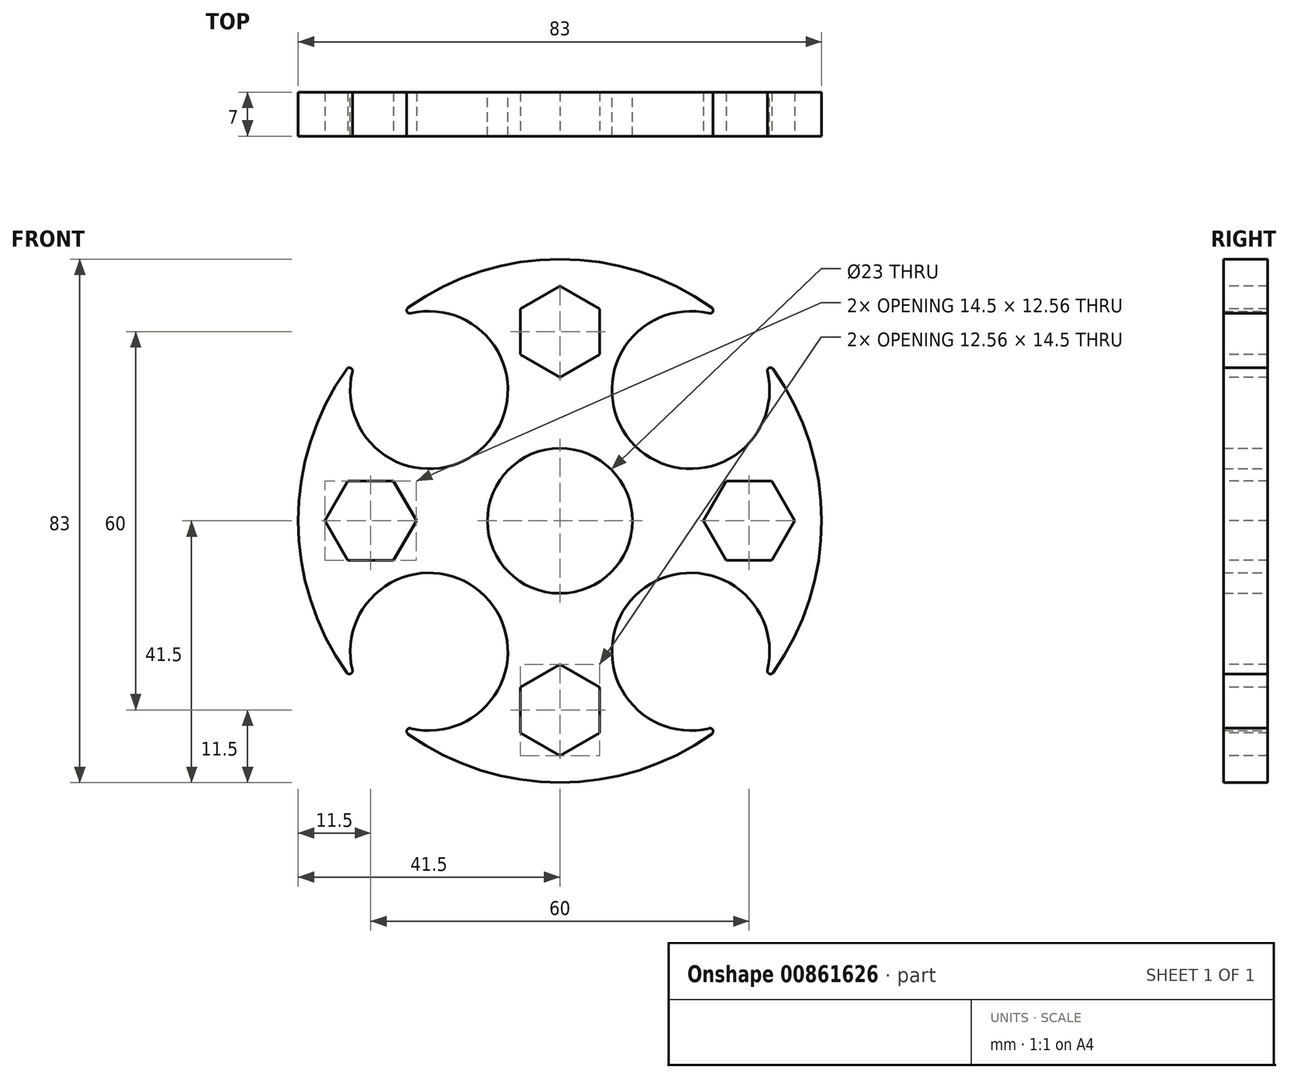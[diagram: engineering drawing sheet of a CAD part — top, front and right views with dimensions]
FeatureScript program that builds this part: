
annotation { "Feature Type Name" : "Feature", "Feature Type Description" : "" }
export const myFeature = defineFeature(function(context is Context, id is Id, definition is map)
    precondition{}
    {
        {
            var Q0;
            Q0=qCreatedBy(makeId("Front.planeOp"),FACE);
            var sketch = newSketch(context, id + "F0", { "sketchPlane" : qUnion([Q0])});
            skCircle(sketch, "E0", {"center": v(0, 0) * mm, "radius": 11.5 * mm});
            skCircle(sketch, "E1", {"center": v(0, 0) * mm, "radius": 41.5 * mm});
            skLineSegment(sketch, "E2", {"start": v(0, 0) * mm, "end": v(0, 41.5) * mm});
            skLineSegment(sketch, "E3", {"start": v(0, 0) * mm, "end": v(41.5, 0) * mm});
            skLineSegment(sketch, "E4", {"start": v(0, 0) * mm, "end": v(0, -41.5) * mm});
            skLineSegment(sketch, "E5", {"start": v(0, 0) * mm, "end": v(-41.5, 0) * mm});
            skLineSegment(sketch, "E6", {"start": v(-20.75, 0) * mm, "end": v(-20.75, 35.94) * mm});
            skLineSegment(sketch, "E7", {"start": v(0, 20.75) * mm, "end": v(-35.94, 20.75) * mm});
            skLineSegment(sketch, "E8", {"start": v(0, 20.75) * mm, "end": v(35.94, 20.75) * mm});
            skLineSegment(sketch, "E9", {"start": v(20.75, 0) * mm, "end": v(20.75, 35.94) * mm});
            skLineSegment(sketch, "E10", {"start": v(0, -20.75) * mm, "end": v(35.94, -20.75) * mm});
            skLineSegment(sketch, "E11", {"start": v(20.75, 0) * mm, "end": v(20.75, -35.94) * mm});
            skLineSegment(sketch, "E12", {"start": v(-20.75, 0) * mm, "end": v(-20.75, -35.94) * mm});
            skLineSegment(sketch, "E13", {"start": v(0, -20.75) * mm, "end": v(-35.94, -20.75) * mm});
            skCircle(sketch, "E14", {"center": v(-20.75, 20.75) * mm, "radius": 12.5 * mm});
            skCircle(sketch, "E15", {"center": v(20.75, 20.75) * mm, "radius": 12.5 * mm});
            skCircle(sketch, "E16", {"center": v(-20.75, -20.75) * mm, "radius": 12.5 * mm});
            skCircle(sketch, "E17", {"center": v(20.75, -20.75) * mm, "radius": 12.5 * mm});
            skSolve(sketch);
        }
        {
            var Q0;
            {var subQ1=sQuery(id+"F0.wireOp",EDGE,"E2");var subQ5=sQuery(id+"F0.wireOp",EDGE,"E1");var subQ6=makeQuery(id+"F0.imprint","INTERSECT",VERTEX,{"derivedFrom":[subQ5,subQ1]});Q0=makeQuery(id+"F0.imprint","IMPRINT",FACE,{"disambiguationData":[TD([[makeQuery(id+"F0.imprint","IMPRINT",EDGE,{"disambiguationData":[TD([[subQ6,-1.0]])],"derivedFrom":subQ5}),1.0]])]});}
            var Q1;
            {var subQ1=sQuery(id+"F0.wireOp",EDGE,"E2");var subQ7=sQuery(id+"F0.wireOp",EDGE,"E1");var subQ9=makeQuery(id+"F0.imprint","INTERSECT",VERTEX,{"derivedFrom":[subQ7,subQ1]});Q1=makeQuery(id+"F0.imprint","IMPRINT",FACE,{"disambiguationData":[TD([[makeQuery(id+"F0.imprint","IMPRINT",EDGE,{"disambiguationData":[TD([[subQ9,1.0]])],"derivedFrom":subQ7}),1.0]])]});}
            var Q2;
            {var subQ3=sQuery(id+"F0.wireOp",EDGE,"E0");var subQ5=sQuery(id+"F0.wireOp",EDGE,"E2");var subQ6=makeQuery(id+"F0.imprint","INTERSECT",VERTEX,{"derivedFrom":[subQ3,subQ5]});Q2=makeQuery(id+"F0.imprint","IMPRINT",FACE,{"disambiguationData":[TD([[makeQuery(id+"F0.imprint","IMPRINT",EDGE,{"disambiguationData":[TD([[subQ6,-1.0]])],"derivedFrom":subQ3}),-1.0]])]});}
            var Q3;
            {var subQ1=sQuery(id+"F0.wireOp",EDGE,"E2");var subQ5=sQuery(id+"F0.wireOp",EDGE,"E0");var subQ6=makeQuery(id+"F0.imprint","INTERSECT",VERTEX,{"derivedFrom":[subQ5,subQ1]});Q3=makeQuery(id+"F0.imprint","IMPRINT",FACE,{"disambiguationData":[TD([[makeQuery(id+"F0.imprint","IMPRINT",EDGE,{"disambiguationData":[TD([[subQ6,1.0]])],"derivedFrom":subQ5}),-1.0]])]});}
            var Q4;
            {var subQ1=sQuery(id+"F0.wireOp",EDGE,"E3");var subQ5=sQuery(id+"F0.wireOp",EDGE,"E1");var subQ6=makeQuery(id+"F0.imprint","INTERSECT",VERTEX,{"derivedFrom":[subQ5,subQ1]});Q4=makeQuery(id+"F0.imprint","IMPRINT",FACE,{"disambiguationData":[TD([[makeQuery(id+"F0.imprint","IMPRINT",EDGE,{"disambiguationData":[TD([[subQ6,-1.0]])],"derivedFrom":subQ5}),1.0]])]});}
            var Q5;
            {var subQ1=sQuery(id+"F0.wireOp",EDGE,"E5");var subQ5=sQuery(id+"F0.wireOp",EDGE,"E1");var subQ6=makeQuery(id+"F0.imprint","INTERSECT",VERTEX,{"derivedFrom":[subQ5,subQ1]});Q5=makeQuery(id+"F0.imprint","IMPRINT",FACE,{"disambiguationData":[TD([[makeQuery(id+"F0.imprint","IMPRINT",EDGE,{"disambiguationData":[TD([[subQ6,1.0]])],"derivedFrom":subQ5}),1.0]])]});}
            var Q6;
            {var subQ1=sQuery(id+"F0.wireOp",EDGE,"E1");var subQ6=sQuery(id+"F0.wireOp",EDGE,"E5");var subQ9=makeQuery(id+"F0.imprint","INTERSECT",VERTEX,{"derivedFrom":[subQ1,subQ6]});Q6=makeQuery(id+"F0.imprint","IMPRINT",FACE,{"disambiguationData":[TD([[makeQuery(id+"F0.imprint","IMPRINT",EDGE,{"disambiguationData":[TD([[subQ9,-1.0]])],"derivedFrom":subQ1}),1.0]])]});}
            var Q7;
            {var subQ1=sQuery(id+"F0.wireOp",EDGE,"E5");var subQ5=sQuery(id+"F0.wireOp",EDGE,"E0");var subQ6=makeQuery(id+"F0.imprint","INTERSECT",VERTEX,{"derivedFrom":[subQ5,subQ1]});Q7=makeQuery(id+"F0.imprint","IMPRINT",FACE,{"disambiguationData":[TD([[makeQuery(id+"F0.imprint","IMPRINT",EDGE,{"disambiguationData":[TD([[subQ6,-1.0]])],"derivedFrom":subQ5}),-1.0]])]});}
            var Q8;
            {var subQ1=sQuery(id+"F0.wireOp",EDGE,"E4");var subQ5=sQuery(id+"F0.wireOp",EDGE,"E1");var subQ6=makeQuery(id+"F0.imprint","INTERSECT",VERTEX,{"derivedFrom":[subQ5,subQ1]});Q8=makeQuery(id+"F0.imprint","IMPRINT",FACE,{"disambiguationData":[TD([[makeQuery(id+"F0.imprint","IMPRINT",EDGE,{"disambiguationData":[TD([[subQ6,1.0]])],"derivedFrom":subQ5}),1.0]])]});}
            var Q9;
            {var subQ1=sQuery(id+"F0.wireOp",EDGE,"E4");var subQ5=sQuery(id+"F0.wireOp",EDGE,"E1");var subQ6=makeQuery(id+"F0.imprint","INTERSECT",VERTEX,{"derivedFrom":[subQ5,subQ1]});Q9=makeQuery(id+"F0.imprint","IMPRINT",FACE,{"disambiguationData":[TD([[makeQuery(id+"F0.imprint","IMPRINT",EDGE,{"disambiguationData":[TD([[subQ6,-1.0]])],"derivedFrom":subQ5}),1.0]])]});}
            var Q10;
            {var subQ5=sQuery(id+"F0.wireOp",EDGE,"E0");var subQ8=sQuery(id+"F0.wireOp",EDGE,"E3");var subQ10=makeQuery(id+"F0.imprint","INTERSECT",VERTEX,{"derivedFrom":[subQ5,subQ8]});Q10=makeQuery(id+"F0.imprint","IMPRINT",FACE,{"disambiguationData":[TD([[makeQuery(id+"F0.imprint","IMPRINT",EDGE,{"disambiguationData":[TD([[subQ10,1.0]])],"derivedFrom":subQ5}),-1.0]])]});}
            var Q11;
            {var subQ1=sQuery(id+"F0.wireOp",EDGE,"E3");var subQ5=sQuery(id+"F0.wireOp",EDGE,"E1");var subQ6=makeQuery(id+"F0.imprint","INTERSECT",VERTEX,{"derivedFrom":[subQ5,subQ1]});Q11=makeQuery(id+"F0.imprint","IMPRINT",FACE,{"disambiguationData":[TD([[makeQuery(id+"F0.imprint","IMPRINT",EDGE,{"disambiguationData":[TD([[subQ6,1.0]])],"derivedFrom":subQ5}),1.0]])]});}
            var Q12;
            {var subQ0=sQuery(id+"F0.wireOp",EDGE,"E11");var subQ1=sQuery(id+"F0.wireOp",EDGE,"E1");var subQ2=makeQuery(id+"F0.imprint","INTERSECT",VERTEX,{"derivedFrom":[subQ1,subQ0]});Q12=makeQuery(id+"F0.imprint","IMPRINT",FACE,{"disambiguationData":[TD([[makeQuery(id+"F0.imprint","IMPRINT",EDGE,{"disambiguationData":[TD([[subQ2,-1.0]])],"derivedFrom":subQ1}),1.0]])]});}
            var Q13;
            {var subQ0=sQuery(id+"F0.wireOp",EDGE,"E10");var subQ1=sQuery(id+"F0.wireOp",EDGE,"E1");var subQ2=makeQuery(id+"F0.imprint","INTERSECT",VERTEX,{"derivedFrom":[subQ1,subQ0]});Q13=makeQuery(id+"F0.imprint","IMPRINT",FACE,{"disambiguationData":[TD([[makeQuery(id+"F0.imprint","IMPRINT",EDGE,{"disambiguationData":[TD([[subQ2,1.0]])],"derivedFrom":subQ1}),1.0]])]});}
            var Q14;
            {var subQ0=sQuery(id+"F0.wireOp",EDGE,"E12");var subQ1=sQuery(id+"F0.wireOp",EDGE,"E1");var subQ2=makeQuery(id+"F0.imprint","INTERSECT",VERTEX,{"derivedFrom":[subQ1,subQ0]});Q14=makeQuery(id+"F0.imprint","IMPRINT",FACE,{"disambiguationData":[TD([[makeQuery(id+"F0.imprint","IMPRINT",EDGE,{"disambiguationData":[TD([[subQ2,1.0]])],"derivedFrom":subQ1}),1.0]])]});}
            var Q15;
            {var subQ0=sQuery(id+"F0.wireOp",EDGE,"E13");var subQ1=sQuery(id+"F0.wireOp",EDGE,"E1");var subQ2=makeQuery(id+"F0.imprint","INTERSECT",VERTEX,{"derivedFrom":[subQ1,subQ0]});Q15=makeQuery(id+"F0.imprint","IMPRINT",FACE,{"disambiguationData":[TD([[makeQuery(id+"F0.imprint","IMPRINT",EDGE,{"disambiguationData":[TD([[subQ2,-1.0]])],"derivedFrom":subQ1}),1.0]])]});}
            var Q16;
            {var subQ0=sQuery(id+"F0.wireOp",EDGE,"E7");var subQ1=sQuery(id+"F0.wireOp",EDGE,"E1");var subQ2=makeQuery(id+"F0.imprint","INTERSECT",VERTEX,{"derivedFrom":[subQ1,subQ0]});Q16=makeQuery(id+"F0.imprint","IMPRINT",FACE,{"disambiguationData":[TD([[makeQuery(id+"F0.imprint","IMPRINT",EDGE,{"disambiguationData":[TD([[subQ2,1.0]])],"derivedFrom":subQ1}),1.0]])]});}
            var Q17;
            {var subQ0=sQuery(id+"F0.wireOp",EDGE,"E6");var subQ1=sQuery(id+"F0.wireOp",EDGE,"E1");var subQ2=makeQuery(id+"F0.imprint","INTERSECT",VERTEX,{"derivedFrom":[subQ1,subQ0]});Q17=makeQuery(id+"F0.imprint","IMPRINT",FACE,{"disambiguationData":[TD([[makeQuery(id+"F0.imprint","IMPRINT",EDGE,{"disambiguationData":[TD([[subQ2,-1.0]])],"derivedFrom":subQ1}),1.0]])]});}
            var Q18;
            {var subQ0=sQuery(id+"F0.wireOp",EDGE,"E9");var subQ1=sQuery(id+"F0.wireOp",EDGE,"E1");var subQ2=makeQuery(id+"F0.imprint","INTERSECT",VERTEX,{"derivedFrom":[subQ1,subQ0]});Q18=makeQuery(id+"F0.imprint","IMPRINT",FACE,{"disambiguationData":[TD([[makeQuery(id+"F0.imprint","IMPRINT",EDGE,{"disambiguationData":[TD([[subQ2,1.0]])],"derivedFrom":subQ1}),1.0]])]});}
            var Q19;
            {var subQ0=sQuery(id+"F0.wireOp",EDGE,"E8");var subQ1=sQuery(id+"F0.wireOp",EDGE,"E1");var subQ2=makeQuery(id+"F0.imprint","INTERSECT",VERTEX,{"derivedFrom":[subQ1,subQ0]});Q19=makeQuery(id+"F0.imprint","IMPRINT",FACE,{"disambiguationData":[TD([[makeQuery(id+"F0.imprint","IMPRINT",EDGE,{"disambiguationData":[TD([[subQ2,-1.0]])],"derivedFrom":subQ1}),1.0]])]});}
            extrude(context, id + "F1", {"entities" : qUnion([Q0, Q1, Q2, Q3, Q4, Q5, Q6, Q7, Q8, Q9, Q10, Q11, Q12, Q13, Q14, Q15, Q16, Q17, Q18, Q19]), "depth" : 7 * mm, "offsetDistance" : 25 * mm});
        }
        {
            var Q0;
            {var subQ0=sQuery(id+"F0.wireOp",EDGE,"E15");var subQ1=sQuery(id+"F0.wireOp",EDGE,"E1");Q0=makeQuery(id+"F1.opExtrude","SWEPT_EDGE",EDGE,{"disambiguationData":[OSD([subQ1,subQ0]),TDD([makeQuery(id+"F0.imprint","INTERSECT",VERTEX,{"disambiguationData":[OD(1.0)],"derivedFrom":[subQ1,subQ0]})])]});}
            var Q1;
            {var subQ0=sQuery(id+"F0.wireOp",EDGE,"E15");var subQ1=sQuery(id+"F0.wireOp",EDGE,"E1");Q1=makeQuery(id+"F1.opExtrude","SWEPT_EDGE",EDGE,{"disambiguationData":[OSD([subQ1,subQ0]),TDD([makeQuery(id+"F0.imprint","INTERSECT",VERTEX,{"disambiguationData":[OD(0.0)],"derivedFrom":[subQ1,subQ0]})])]});}
            var Q2;
            {var subQ0=sQuery(id+"F0.wireOp",EDGE,"E17");var subQ1=sQuery(id+"F0.wireOp",EDGE,"E1");Q2=makeQuery(id+"F1.opExtrude","SWEPT_EDGE",EDGE,{"disambiguationData":[OSD([subQ1,subQ0]),TDD([makeQuery(id+"F0.imprint","INTERSECT",VERTEX,{"disambiguationData":[OD(1.0)],"derivedFrom":[subQ1,subQ0]})])]});}
            var Q3;
            {var subQ0=sQuery(id+"F0.wireOp",EDGE,"E17");var subQ1=sQuery(id+"F0.wireOp",EDGE,"E1");Q3=makeQuery(id+"F1.opExtrude","SWEPT_EDGE",EDGE,{"disambiguationData":[OSD([subQ1,subQ0]),TDD([makeQuery(id+"F0.imprint","INTERSECT",VERTEX,{"disambiguationData":[OD(0.0)],"derivedFrom":[subQ1,subQ0]})])]});}
            var Q4;
            {var subQ0=sQuery(id+"F0.wireOp",EDGE,"E16");var subQ1=sQuery(id+"F0.wireOp",EDGE,"E1");Q4=makeQuery(id+"F1.opExtrude","SWEPT_EDGE",EDGE,{"disambiguationData":[OSD([subQ1,subQ0]),TDD([makeQuery(id+"F0.imprint","INTERSECT",VERTEX,{"disambiguationData":[OD(1.0)],"derivedFrom":[subQ1,subQ0]})])]});}
            var Q5;
            {var subQ0=sQuery(id+"F0.wireOp",EDGE,"E16");var subQ1=sQuery(id+"F0.wireOp",EDGE,"E1");Q5=makeQuery(id+"F1.opExtrude","SWEPT_EDGE",EDGE,{"disambiguationData":[OSD([subQ1,subQ0]),TDD([makeQuery(id+"F0.imprint","INTERSECT",VERTEX,{"disambiguationData":[OD(0.0)],"derivedFrom":[subQ1,subQ0]})])]});}
            var Q6;
            {var subQ0=sQuery(id+"F0.wireOp",EDGE,"E14");var subQ1=sQuery(id+"F0.wireOp",EDGE,"E1");Q6=makeQuery(id+"F1.opExtrude","SWEPT_EDGE",EDGE,{"disambiguationData":[OSD([subQ1,subQ0]),TDD([makeQuery(id+"F0.imprint","INTERSECT",VERTEX,{"disambiguationData":[OD(0.0)],"derivedFrom":[subQ1,subQ0]})])]});}
            var Q7;
            {var subQ0=sQuery(id+"F0.wireOp",EDGE,"E14");var subQ1=sQuery(id+"F0.wireOp",EDGE,"E1");Q7=makeQuery(id+"F1.opExtrude","SWEPT_EDGE",EDGE,{"disambiguationData":[OSD([subQ1,subQ0]),TDD([makeQuery(id+"F0.imprint","INTERSECT",VERTEX,{"disambiguationData":[OD(1.0)],"derivedFrom":[subQ1,subQ0]})])]});}
            fillet(context, id + "F2", {"entities" : qUnion([Q0, Q1, Q2, Q3, Q4, Q5, Q6, Q7]), "radius" : 0.5 * mm, "tangentPropagation" : true, "allowEdgeOverflow" : false});
        }
        {
            var Q0;
            Q0=makeQuery(id+"F1.opExtrude","CAP_FACE",FACE,{"disambiguationData":[OSD([sQuery(id+"F0.wireOp",EDGE,"E0"),sQuery(id+"F0.wireOp",EDGE,"E1"),sQuery(id+"F0.wireOp",EDGE,"E14"),sQuery(id+"F0.wireOp",EDGE,"E15"),sQuery(id+"F0.wireOp",EDGE,"E16"),sQuery(id+"F0.wireOp",EDGE,"E17")])],"isStart":false});
            var sketch = newSketch(context, id + "F3", { "sketchPlane" : qUnion([Q0])});
            skCircle(sketch, "E18.cCircle", {"center": v(0, 30) * mm, "radius": 7.25 * mm, "construction": true});
            skLineSegment(sketch, "E18.0", {"start": v(0, 37.25) * mm, "end": v(6.28, 33.62) * mm});
            skLineSegment(sketch, "E18.1", {"start": v(6.28, 33.62) * mm, "end": v(6.28, 26.38) * mm});
            skLineSegment(sketch, "E18.2", {"start": v(6.28, 26.38) * mm, "end": v(0, 22.75) * mm});
            skLineSegment(sketch, "E18.3", {"start": v(0, 22.75) * mm, "end": v(-6.28, 26.38) * mm});
            skLineSegment(sketch, "E18.4", {"start": v(-6.28, 26.37) * mm, "end": v(-6.28, 33.62) * mm});
            skLineSegment(sketch, "E18.5", {"start": v(-6.28, 33.62) * mm, "end": v(0, 37.25) * mm});
            skLineSegment(sketch, "E19.1.0", {"start": v(-37.25, 0) * mm, "end": v(-33.62, 6.28) * mm});
            skLineSegment(sketch, "E19.1.1", {"start": v(-26.38, 6.28) * mm, "end": v(-22.75, 0) * mm});
            skLineSegment(sketch, "E19.1.2", {"start": v(-22.75, 0) * mm, "end": v(-26.38, -6.28) * mm});
            skLineSegment(sketch, "E19.1.3", {"start": v(-33.62, -6.28) * mm, "end": v(-37.25, 0) * mm});
            skLineSegment(sketch, "E19.1.4", {"start": v(-26.37, -6.28) * mm, "end": v(-33.62, -6.28) * mm});
            skLineSegment(sketch, "E19.1.5", {"start": v(-33.62, 6.28) * mm, "end": v(-26.38, 6.28) * mm});
            skCircle(sketch, "E19.1.6", {"center": v(-30, 0) * mm, "radius": 7.25 * mm, "construction": true});
            skLineSegment(sketch, "E19.2.0", {"start": v(0, -37.25) * mm, "end": v(-6.28, -33.62) * mm});
            skLineSegment(sketch, "E19.2.1", {"start": v(-6.28, -26.38) * mm, "end": v(0, -22.75) * mm});
            skLineSegment(sketch, "E19.2.2", {"start": v(0, -22.75) * mm, "end": v(6.28, -26.38) * mm});
            skLineSegment(sketch, "E19.2.3", {"start": v(6.28, -33.62) * mm, "end": v(0, -37.25) * mm});
            skLineSegment(sketch, "E19.2.4", {"start": v(6.28, -26.37) * mm, "end": v(6.28, -33.62) * mm});
            skLineSegment(sketch, "E19.2.5", {"start": v(-6.28, -33.62) * mm, "end": v(-6.28, -26.38) * mm});
            skCircle(sketch, "E19.2.6", {"center": v(0, -30) * mm, "radius": 7.25 * mm, "construction": true});
            skLineSegment(sketch, "E19.3.0", {"start": v(37.25, 0) * mm, "end": v(33.62, -6.28) * mm});
            skLineSegment(sketch, "E19.3.1", {"start": v(26.38, -6.28) * mm, "end": v(22.75, 0) * mm});
            skLineSegment(sketch, "E19.3.2", {"start": v(22.75, 0) * mm, "end": v(26.38, 6.28) * mm});
            skLineSegment(sketch, "E19.3.3", {"start": v(33.62, 6.28) * mm, "end": v(37.25, 0) * mm});
            skLineSegment(sketch, "E19.3.4", {"start": v(26.37, 6.28) * mm, "end": v(33.62, 6.28) * mm});
            skLineSegment(sketch, "E19.3.5", {"start": v(33.62, -6.28) * mm, "end": v(26.38, -6.28) * mm});
            skCircle(sketch, "E19.3.6", {"center": v(30, 0) * mm, "radius": 7.25 * mm, "construction": true});
            skPoint(sketch, "E19.center", {"position": v(0, 0) * mm});
            skSolve(sketch);
        }
        {
            var Q0;
            Q0=makeQuery(id+"F3.imprint","IMPRINT",FACE,{"disambiguationData":[TD([[makeQuery(id+"F3.imprint","IMPRINT",EDGE,{"derivedFrom":sQuery(id+"F3.wireOp",EDGE,"E18.0")}),-1.0]])]});
            var Q1;
            Q1=makeQuery(id+"F3.imprint","IMPRINT",FACE,{"disambiguationData":[TD([[makeQuery(id+"F3.imprint","IMPRINT",EDGE,{"derivedFrom":sQuery(id+"F3.wireOp",EDGE,"E19.3.0")}),-1.0]])]});
            var Q2;
            Q2=makeQuery(id+"F3.imprint","IMPRINT",FACE,{"disambiguationData":[TD([[makeQuery(id+"F3.imprint","IMPRINT",EDGE,{"derivedFrom":sQuery(id+"F3.wireOp",EDGE,"E19.2.0")}),-1.0]])]});
            var Q3;
            Q3=makeQuery(id+"F3.imprint","IMPRINT",FACE,{"disambiguationData":[TD([[makeQuery(id+"F3.imprint","IMPRINT",EDGE,{"derivedFrom":sQuery(id+"F3.wireOp",EDGE,"E19.1.0")}),-1.0]])]});
            extrude(context, id + "F4", {"entities" : qUnion([Q0, Q1, Q2, Q3]), "operationType" : NewBodyOperationType.REMOVE, "oppositeDirection" : true, "depth" : 25 * mm, "offsetDistance" : 25 * mm});
        }
    });
